# Revit family: IS_Conca_T3818_BIM_UK
name_source: partatom
category: Plumbing Fixtures
revit_build: Autodesk Revit 2017 (Build: 20160225_1515(x64)
units: mm (PartAtom-declared; Revit-internal decimal feet)

## family parameters
Always vertical = No
Cut with Voids When Loaded = No
OmniClass Number = 23.45.05.14.14
OmniClass Title = Sinks/Lavatories
Part Type = Normal
Room Calculation Point = No
Round Connector Dimension = Use Diameter
Shared = No
Work Plane-Based = No

## types (1)
- T381801 - Conca New consolle basin 60 1TH OF GR
    AreaUnits = millimeters
    AssetType = Fixed
    BIMObjectName = ISI_IdealStandard_CounterTopWashBasins_Conca_T3818
    BarCode = 8014140458340
    Brand = Ideal Standard
    CisternCapacity = 0.00 m³
    Color = White
    CurrencyUnit = £
    Description = Conca Rectangular washbasin for suspended or countertop installation,  600x450mm with overflow,1 tap hole. Fixedup.White Finish
    DurationUnit = year
    ExpectedLife = 90
    Features = Rectangular washbasin for suspended or countertop installation,  600x450mm with overflow,1 tap hole. Fixedup.White Finish
    Finish = White
    FlushRate = 0.00 m³
    FlushingRate = 0
    HasGrabHandles = No
    HasIntegralShutOffDevice = No
    HasTray = No
    IfcExportAs = IfcSanitaryTerminalType
    IfcExportType = WASHHANDBASIN
    InletConnectionSize = 0 mm  [stored 0 ft]
    Installation instructions = www.idealspec.co.uk/resources.html
    InstallationInstructions = www.idealspec.co.uk/resources.html
    IsAutomaticFlush = No
    IsBuiltIn = No
    IsHighPressure = No
    IsSingleFlush = No
    LinearUnits = millimeters
    MainColor = White
    MaintenanceInformation = https://www.ideal-standard.co.uk
    ManufacturerURL = www.idealspec.co.uk
    Material = Fine fireclay
    MaterialThickness = 0 mm  [stored 0 ft]
    Model = T381801
    ModelNumber = T3818
    Name = ISI_CounterTopWashBasins_Conca_T3818_IdealStandard
    NominalDepth = 450 mm
    NominalHeight = 168 mm
    NominalWidth = 600 mm  [stored 1.9685 ft]
    OutletConnectionSize = 0 mm  [stored 0 ft]
    Product group = Wash-Basin
    ProductInformation = https://www.idealspec.co.uk
    SeatHasCover = No
    Shape = Sculptured
    Size = 600 x 450 x 168 mm
    Space = Internal
    SpareParts = www.fastpart-spares.co.uk
    SpilloverLevel = 0 mm  [stored 0 ft]
    URL = https://www.ideal-standard.co.uk
    Uniclass 2015 Code = Pr_40_20_96_18
    Uniclass 2015 Name = Counter top wash basins
    Uniclass2015Code = Pr_40_20_96_18
    Uniclass2015Title = Counter top wash basins
    Uniclass2015Version = v1.1
    Version = 1
    VolumeUnits = Litres
    WarrantyDescription = Manufacturers Warranty
    WarrantyDurationParts = 99
    WarrantyDurationUnit = year
    WarrantyGuarantorLabor = n/s
    WashHandBasinMounting = CounterTop
    WashHandBasinType = Hand Rinse

note: [stored X ft] marks values corroborated as IEEE doubles in the binary element streams (Revit-internal decimal feet)

## geometry (parser evidence)
native form markers: Sweep x1
no freeform markers — native parametric forms only
